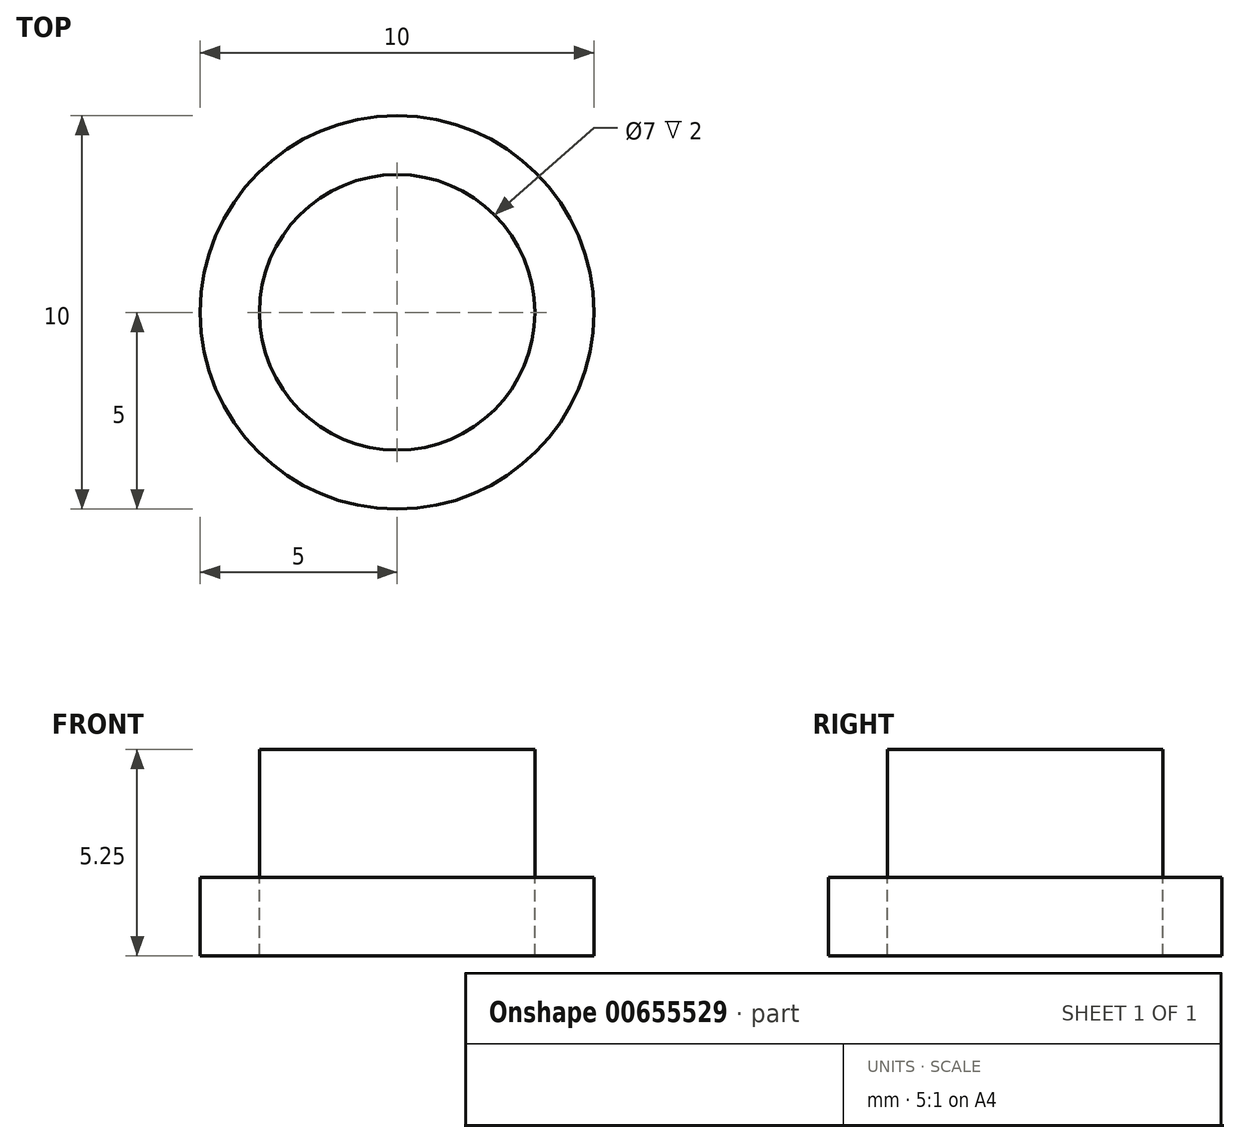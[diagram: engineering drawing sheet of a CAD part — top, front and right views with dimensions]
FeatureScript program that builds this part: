
annotation { "Feature Type Name" : "Feature", "Feature Type Description" : "" }
export const myFeature = defineFeature(function(context is Context, id is Id, definition is map)
    precondition{}
    {
        {
            var Q0;
            Q0=qCreatedBy(makeId("Top.planeOp"),FACE);
            var sketch = newSketch(context, id + "F0", { "sketchPlane" : qUnion([Q0])});
            skCircle(sketch, "E0", {"center": v(0, 0) * mm, "radius": 11 * mm});
            skCircle(sketch, "E1", {"center": v(0, 0) * mm, "radius": 5 * mm});
            skCircle(sketch, "E2", {"center": v(0, 0) * mm, "radius": 3.5 * mm});
            skSolve(sketch);
        }
        {
            var Q0;
            Q0=makeQuery(id+"F0.imprint","IMPRINT",FACE,{"disambiguationData":[TD([[makeQuery(id+"F0.imprint","IMPRINT",EDGE,{"derivedFrom":sQuery(id+"F0.wireOp",EDGE,"E2")}),1.0]])]});
            var Q1;
            Q1=sQuery(id+"F0.wireOp",EDGE,"E2");
            extrude(context, id + "F1", {"entities" : qUnion([Q0]), "surfaceEntities" : qUnion([Q1]), "depth" : 3.25 * mm, "offsetDistance" : 25.4 * mm});
        }
        {
            var Q0;
            Q0=makeQuery(id+"F0.imprint","IMPRINT",FACE,{"disambiguationData":[TD([[makeQuery(id+"F0.imprint","IMPRINT",EDGE,{"derivedFrom":sQuery(id+"F0.wireOp",EDGE,"E1")}),1.0]])]});
            var Q1;
            Q1=sQuery(id+"F0.wireOp",EDGE,"E1");
            extrude(context, id + "F2", {"entities" : qUnion([Q0]), "surfaceEntities" : qUnion([Q1]), "oppositeDirection" : true, "depth" : 2 * mm, "offsetDistance" : 25.4 * mm, "hasSecondDirection" : true, "secondDirectionOppositeDirection" : false, "secondDirectionDepth" : 0 * mm});
        }
    });
